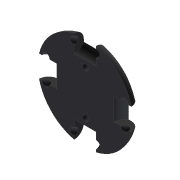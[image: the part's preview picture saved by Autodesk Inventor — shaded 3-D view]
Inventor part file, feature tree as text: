
AUTODESK INVENTOR PART (.ipt)
format: ipt  version: 2017 (Build 210142000, 142)  size: 178,688 bytes
history: native  units: mm
features: sketch x4, extrude x2, fillet x1, revolve x1, pattern_circular x1, hole x1
ambient origin geometry x8: Origin, YZ Plane, XZ Plane, XY Plane, X Axis, Y Axis, Z Axis, Center Point
bodies: Solid1 (feature_tree)
feature tree (10):
  extrude  "Extrusion1"  Depth=6.0mm TaperAngle=0.0deg
  fillet  "Fillet1"  Radius=6.0mm
  revolve  "Revolution1"  [1 undecoded]
  pattern_circular  "Circular Pattern1"  [2 undecoded]
  hole  "Hole1"  [1 undecoded]
  extrude  "Extrusion2"  Depth=3.0mm TaperAngle=360.0deg
  sketch  "Sketch1"  dims[d0=60.0mm d1=6.0mm d2=0.0mm d3=6.0mm]
  sketch  "Sketch2"  dims[d4=14.0mm d5=7.0mm]
  sketch  "Sketch3"  dims[d6=18.0mm]
  sketch  "Sketch4"  dims[d7=5.0mm d8=5.0mm d9=90.0deg d10=40.0mm d11=360.0deg d13=14.0mm d14=14.0mm d15=4.0mm d16=6.0mm d17=4.0mm d18=2.0mm d19=90.0deg d20=8.0mm d21=20.594885mm d22=5.5mm d23=5.5mm d24=3.0mm d25=0.0mm]
note: 4 required parameter values undecoded (feature->parameter linkage not recoverable at this tier; creation-order binding heuristic only, values carry confidence <= 0.55)